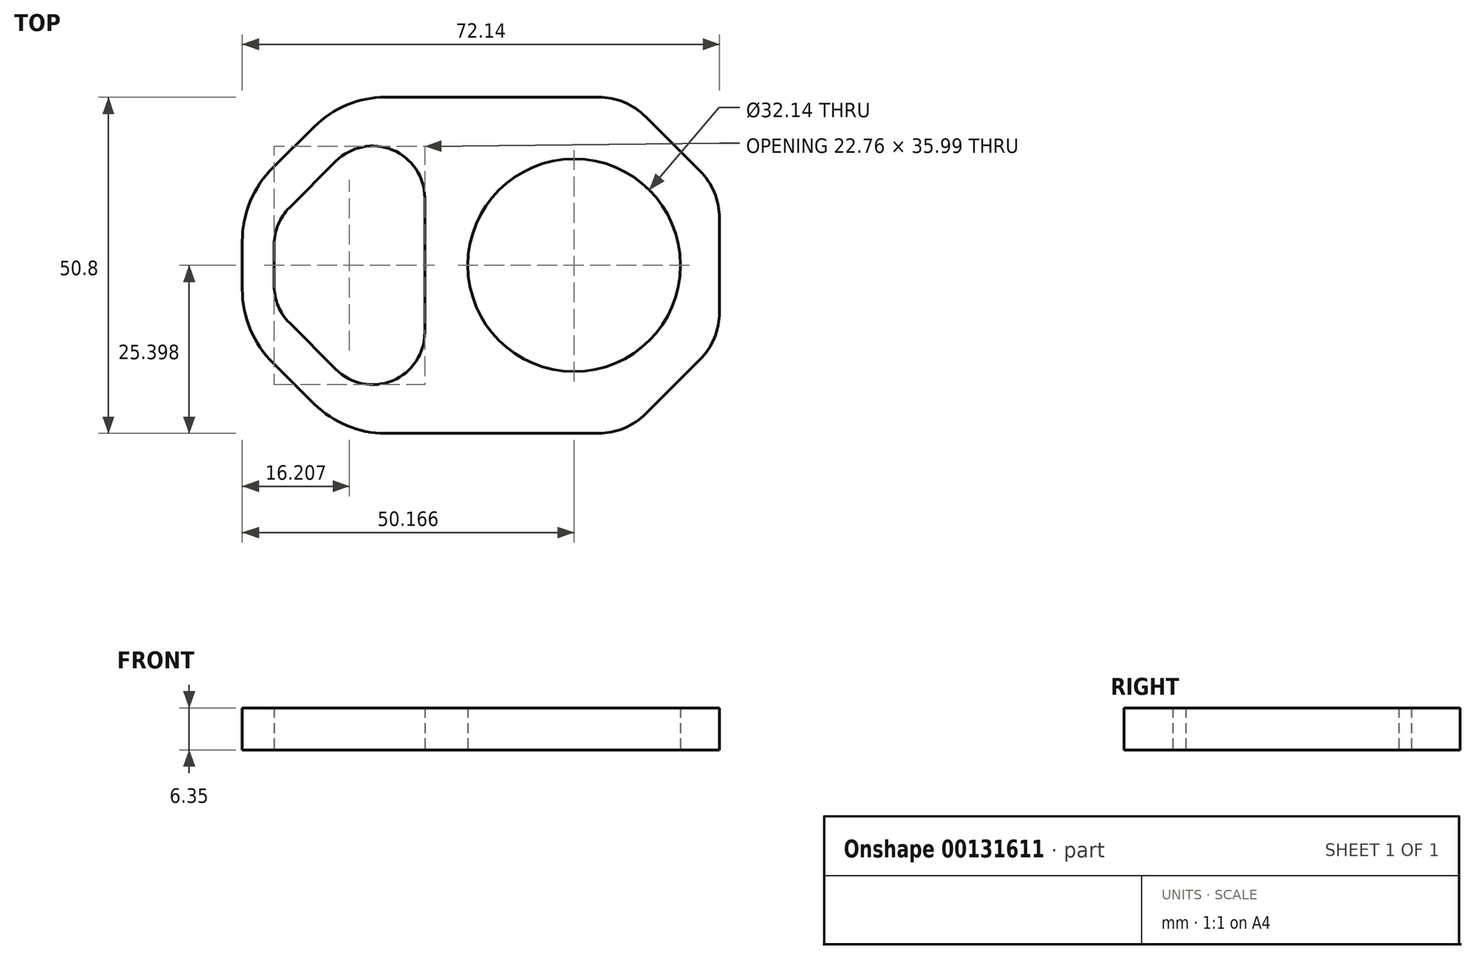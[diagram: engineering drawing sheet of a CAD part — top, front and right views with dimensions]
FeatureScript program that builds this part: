
annotation { "Feature Type Name" : "Feature", "Feature Type Description" : "" }
export const myFeature = defineFeature(function(context is Context, id is Id, definition is map)
    precondition{}
    {
        {
            var Q0;
            Q0=qCreatedBy(makeId("Top.planeOp"),FACE);
            var sketch = newSketch(context, id + "F0", { "sketchPlane" : qUnion([Q0])});
            skCircle(sketch, "E0", {"center": v(50.44, -25.61) * mm, "radius": 16.07 * mm});
            skPoint(sketch, "E1", {"position": v(72.4, -36.91) * mm});
            skPoint(sketch, "E2", {"position": v(58.31, -51.01) * mm});
            skPoint(sketch, "E3.orphan", {"position": v(72.4, -51.01) * mm});
            skLineSegment(sketch, "E4.bottom", {"start": v(72.4, -32.7) * mm, "end": v(72.4, -18.52) * mm});
            skLineSegment(sketch, "E4.top", {"start": v(0.27, -29.21) * mm, "end": v(0.27, -22.01) * mm});
            skLineSegment(sketch, "E4.left", {"start": v(54.1, -51.01) * mm, "end": v(21.91, -51.01) * mm});
            skLineSegment(sketch, "E4.right", {"start": v(54.1, -0.21) * mm, "end": v(21.91, -0.21) * mm});
            skLineSegment(sketch, "E5", {"start": v(61.29, -48.04) * mm, "end": v(69.43, -39.9) * mm});
            skArc(sketch, "E6.filletArc", {"start": v(54.1, -51.01) * mm, "mid": v(58, -50.24) * mm, "end": v(61.29, -48.04) * mm});
            skArc(sketch, "E7.filletArc", {"start": v(69.43, -39.9) * mm, "mid": v(71.63, -36.6) * mm, "end": v(72.4, -32.7) * mm});
            skArc(sketch, "E8.MirrorCS", {"start": v(54.1, -0.21) * mm, "mid": v(58, -0.98) * mm, "end": v(61.29, -3.19) * mm});
            skLineSegment(sketch, "E9.MirrorCS", {"start": v(61.29, -3.19) * mm, "end": v(69.43, -11.33) * mm});
            skArc(sketch, "E10.MirrorCS", {"start": v(69.43, -11.33) * mm, "mid": v(71.63, -14.63) * mm, "end": v(72.4, -18.52) * mm});
            skPoint(sketch, "E11", {"position": v(15.64, -51.01) * mm});
            skPoint(sketch, "E12.MirrorP", {"position": v(15.64, -0.21) * mm});
            skPoint(sketch, "E13", {"position": v(0.27, -35.77) * mm});
            skLineSegment(sketch, "E14", {"start": v(11.18, -46.6) * mm, "end": v(4.93, -40.4) * mm});
            skArc(sketch, "E15.filletArc", {"start": v(11.18, -46.6) * mm, "mid": v(16.11, -49.86) * mm, "end": v(21.91, -51.01) * mm});
            skArc(sketch, "E16.filletArc", {"start": v(0.27, -29.21) * mm, "mid": v(1.48, -35.27) * mm, "end": v(4.93, -40.4) * mm});
            skArc(sketch, "E17.MirrorCS", {"start": v(11.18, -4.63) * mm, "mid": v(16.11, -1.36) * mm, "end": v(21.91, -0.21) * mm});
            skLineSegment(sketch, "E18.MirrorCS", {"start": v(11.18, -4.63) * mm, "end": v(4.93, -10.83) * mm});
            skArc(sketch, "E19.MirrorCS", {"start": v(0.27, -22.01) * mm, "mid": v(1.48, -15.96) * mm, "end": v(4.93, -10.83) * mm});
            skLineSegment(sketch, "E20", {"start": v(19.98, -35.77) * mm, "end": v(27.86, -35.77) * mm});
            skLineSegment(sketch, "E21", {"start": v(27.86, -35.77) * mm, "end": v(27.86, -15.45) * mm});
            skLineSegment(sketch, "E22", {"start": v(5.1, -28.76) * mm, "end": v(5.1, -22.46) * mm});
            skLineSegment(sketch, "E23", {"start": v(19.98, -35.77) * mm, "end": v(19.98, -43.65) * mm});
            skLineSegment(sketch, "E24", {"start": v(14.41, -41.34) * mm, "end": v(7.4, -34.33) * mm});
            skLineSegment(sketch, "E25.MirrorCS", {"start": v(14.41, -9.88) * mm, "end": v(7.4, -16.9) * mm});
            skArc(sketch, "E26.trimOffspring", {"start": v(14.41, -41.34) * mm, "mid": v(23, -43.05) * mm, "end": v(27.86, -35.77) * mm});
            skArc(sketch, "E27.trimOffspring", {"start": v(5.1, -22.46) * mm, "mid": v(5.7, -19.45) * mm, "end": v(7.4, -16.9) * mm});
            skArc(sketch, "E28.trimOffspring", {"start": v(5.1, -28.76) * mm, "mid": v(5.7, -31.77) * mm, "end": v(7.4, -34.33) * mm});
            skArc(sketch, "E29.trimOffspring", {"start": v(14.41, -9.88) * mm, "mid": v(23, -8.18) * mm, "end": v(27.86, -15.45) * mm});
            skPoint(sketch, "E30.trimOffspring.end.orphan", {"position": v(74.5, -25.61) * mm});
            skPoint(sketch, "E31.start.orphan", {"position": v(-2.05, -25.61) * mm});
            skSolve(sketch);
        }
        {
            var Q0;
            Q0=makeQuery(id+"F0.imprint","IMPRINT",FACE,{"disambiguationData":[TD([[makeQuery(id+"F0.imprint","IMPRINT",EDGE,{"derivedFrom":sQuery(id+"F0.wireOp",EDGE,"E0")}),-1.0]])]});
            extrude(context, id + "F1", {"entities" : qUnion([Q0]), "depth" : 6.35 * mm});
        }
    });
